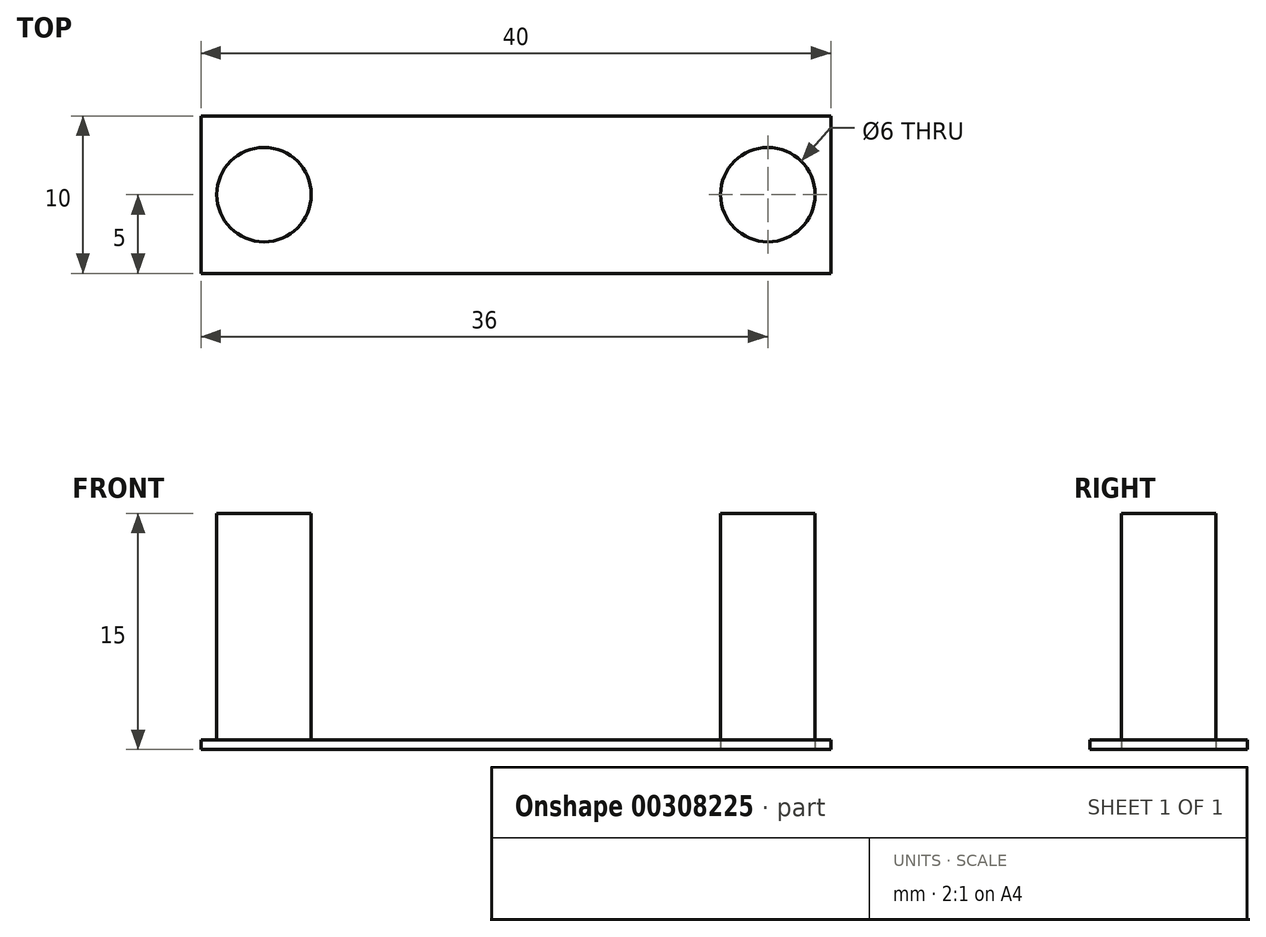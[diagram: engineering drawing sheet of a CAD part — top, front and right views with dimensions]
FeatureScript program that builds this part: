
annotation { "Feature Type Name" : "Feature", "Feature Type Description" : "" }
export const myFeature = defineFeature(function(context is Context, id is Id, definition is map)
    precondition{}
    {
        {
            var Q0;
            Q0=qCreatedBy(makeId("Top.planeOp"),FACE);
            var sketch = newSketch(context, id + "F0", { "sketchPlane" : qUnion([Q0])});
            skLineSegment(sketch, "E0.bottom", {"start": v(20, 5) * mm, "end": v(-20, 5) * mm});
            skLineSegment(sketch, "E0.top", {"start": v(20, -5) * mm, "end": v(-20, -5) * mm});
            skLineSegment(sketch, "E0.left", {"start": v(20, 5) * mm, "end": v(20, -5) * mm});
            skLineSegment(sketch, "E0.right", {"start": v(-20, 5) * mm, "end": v(-20, -5) * mm});
            skPoint(sketch, "E0.middle", {"position": v(0, 0) * mm});
            skCircle(sketch, "E1", {"center": v(-16, 0) * mm, "radius": 3 * mm});
            skCircle(sketch, "E2", {"center": v(16, 0) * mm, "radius": 3 * mm});
            skSolve(sketch);
        }
        {
            var Q0;
            Q0=makeQuery(id+"F0.imprint","IMPRINT",FACE,{"disambiguationData":[TD([[makeQuery(id+"F0.imprint","IMPRINT",EDGE,{"derivedFrom":sQuery(id+"F0.wireOp",EDGE,"E0.bottom")}),1.0]])]});
            extrude(context, id + "F1", {"entities" : qUnion([Q0]), "depth" : .6 * mm, "offsetDistance" : 25 * mm});
        }
        {
            var Q0;
            Q0=makeQuery(id+"F0.imprint","IMPRINT",FACE,{"disambiguationData":[TD([[makeQuery(id+"F0.imprint","IMPRINT",EDGE,{"derivedFrom":sQuery(id+"F0.wireOp",EDGE,"E1")}),1.0]])]});
            extrude(context, id + "F2", {"entities" : qUnion([Q0]), "operationType" : NewBodyOperationType.ADD, "depth" : 15 * mm, "offsetDistance" : 25 * mm});
        }
        {
            var Q0;
            Q0=makeQuery(id+"F0.imprint","IMPRINT",FACE,{"disambiguationData":[TD([[makeQuery(id+"F0.imprint","IMPRINT",EDGE,{"derivedFrom":sQuery(id+"F0.wireOp",EDGE,"E2")}),1.0]])]});
            extrude(context, id + "F3", {"entities" : qUnion([Q0]), "depth" : 15 * mm, "offsetDistance" : 25 * mm});
        }
    });
